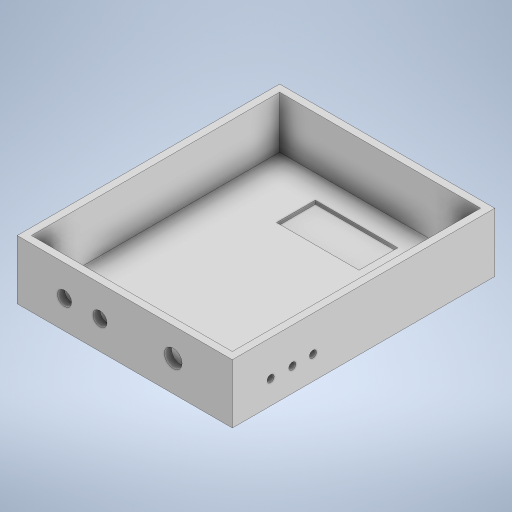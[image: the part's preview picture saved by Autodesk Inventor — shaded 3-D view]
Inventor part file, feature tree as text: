
AUTODESK INVENTOR PART (.ipt)
format: ipt  version: 2024 (Build 280153000, 153)  size: 626,176 bytes
history: native  units: mm
features: extrude x5, other x1, sketch x1
ambient origin geometry x8: Origin, YZ Plane, XZ Plane, XY Plane, X Axis, Y Axis, Z Axis, Center Point
bodies: Body1 (feature_tree)
feature tree (7):
  other  "Sólido1"
  extrude  "Extrusão1"  Depth=3.0mm
  extrude  "Extrusão2"  Depth=3.0mm
  extrude  "Extrusão3"  Depth=3.0mm
  extrude  "Extrusão4"  Depth=85.0mm
  extrude  "Extrusão5"  Depth=105.0mm
  sketch  "Esboço3"  dims[d0=3.0mm d1=3.0mm d2=3.0mm d3=3.0mm d4=85.0mm d5=105.0mm d6=3.0mm d7=0.0mm d8=25.0mm d9=0.0mm d10=6.0mm d11=7.5mm d12=30.0mm d13=0.0mm d14=3.0mm d15=3.0mm d16=3.0mm d17=10.0mm d18=0.0mm d19=34.9mm d20=16.4mm d21=1.5mm d22=0.0mm d23=25.0mm d24=10.0mm d25=20.0mm d26=25.0mm d27=6.0mm d28=15.0mm d29=12.0mm d30=13.0mm d31=12.0mm d32=10.0mm d33=10.0mm d34=10.0mm]
